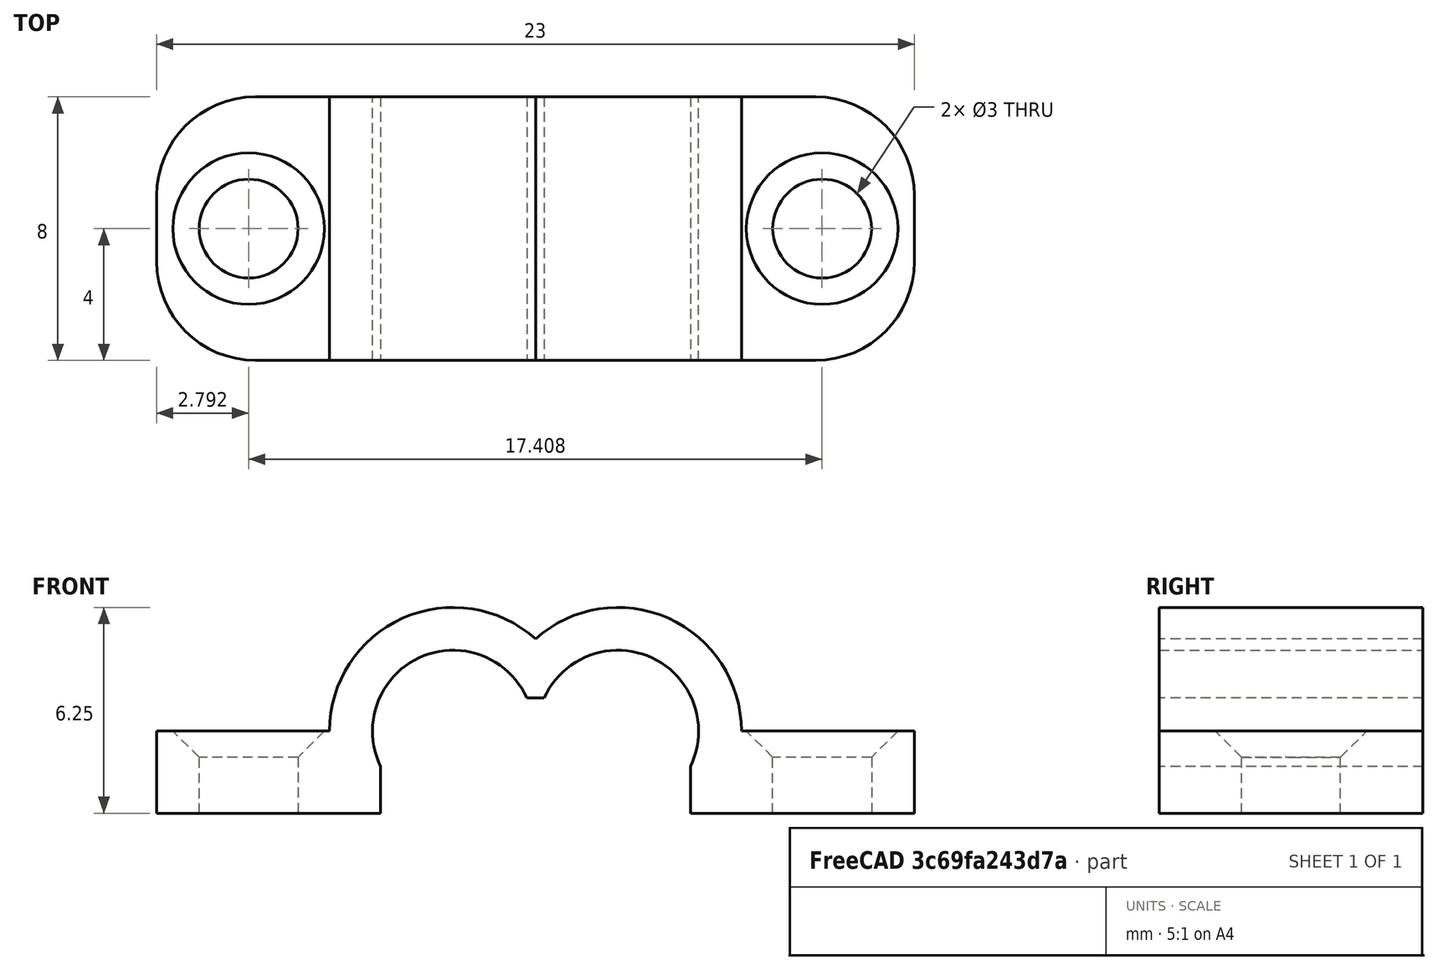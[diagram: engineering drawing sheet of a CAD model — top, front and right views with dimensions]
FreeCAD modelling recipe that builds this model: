
FCSTD DOCUMENT  (FreeCAD 0.21R32110 (Git))
Label: 2Cable_Clip_4_7mm
License: All rights reserved
LicenseURL: http://en.wikipedia.org/wiki/All_rights_reserved
objects: Sketcher::SketchObject×2, PartDesign::Pad×1, PartDesign::Pocket×1, PartDesign::Chamfer×1, PartDesign::Fillet×1, PartDesign::Body×1, App::Part×1
note: 11 computed .brp shape members not serialized (recipe doc carries the construction recipe); baked Part::Feature solids carry a one-line shape summary decoded from their .brp

FEATURE [Sketcher::SketchObject] Sketch
  FullyConstrained = false
  MapMode = 5
  Placement = pos=(0,0,0) rot=(1,0,0;1.5708rad)
  Support = -> [XZ_Plane001]
  sketch-geometry (14):
    g0: ArcOfCircle CenterX=9.25 CenterY=2.5 CenterZ=0 NormalX=0 NormalY=0 NormalZ=1 AngleXU=0 Radius=2.45 StartAngle=0.420441 EndAngle=3.14159
    g1: LineSegment StartX=0 StartY=0 StartZ=0 EndX=6.8 EndY=0 EndZ=0
    g2: LineSegment StartX=23.5 StartY=0 StartZ=0 EndX=23.5 EndY=2.5 EndZ=0
    g3: LineSegment StartX=0 StartY=2.5 StartZ=0 EndX=0 EndY=0 EndZ=0
    g4: LineSegment StartX=5.25 StartY=2.5 StartZ=0 EndX=0 EndY=2.5 EndZ=0
    g5: LineSegment StartX=6.8 StartY=2.5 StartZ=0 EndX=6.8 EndY=0 EndZ=0
    g6: LineSegment StartX=16.7 StartY=0 StartZ=0 EndX=23.5 EndY=0 EndZ=0
    g7: LineSegment StartX=10 StartY=3.5 StartZ=0 EndX=20 EndY=3.5 EndZ=0
    g8: ArcOfCircle CenterX=14.25 CenterY=2.5 CenterZ=0 NormalX=0 NormalY=0 NormalZ=1 AngleXU=0 Radius=2.45 StartAngle=4.07627e-08 EndAngle=2.72115
    g9: LineSegment StartX=23.5 StartY=2.5 StartZ=0 EndX=18.25 EndY=2.5 EndZ=0
    g10: ArcOfCircle CenterX=9.25 CenterY=2.5 CenterZ=0 NormalX=0 NormalY=0 NormalZ=1 AngleXU=0 Radius=4 StartAngle=0.895665 EndAngle=3.14159
    g11: LineSegment StartX=16.7 StartY=0 StartZ=0 EndX=16.7 EndY=2.5 EndZ=0
    g12: LineSegment StartX=11.4866 StartY=3.5 StartZ=0 EndX=11.7634 EndY=3.5 EndZ=0
    g13: ArcOfCircle CenterX=14.25 CenterY=2.5 CenterZ=0 NormalX=0 NormalY=0 NormalZ=1 AngleXU=0 Radius=4 StartAngle=0 EndAngle=2.24593
  constraints (42):
    c: Diameter(g0) = 4.9
    c: Coincident(g6,g2)
    c: Coincident(g4,g3)
    c: Coincident(g3,g1)
    c: Horizontal(g1)
    c: Vertical(g2)
    c: Vertical(g3)
    c: Coincident(g1,g-1)
    c: Coincident(g4,g10)
    c: Vertical(g5)
    c: Coincident(g5,g0)
    c: Coincident(g5,g1)
    c: Distance(g3) = 2.5
    c: Equal(g3,g2)
    c: DistanceY(g0) = 2.5
    c: Horizontal(g6)
    c: Horizontal(g4)
    c: Horizontal(g7)
    c: Coincident(g9,g2)
    c: Horizontal(g9)
    c: Distance(g1) = 6.8
    c: Equal(g1,g6)
    c: PointOnObject(g12,g7)
    c: PointOnObject(g0,g7)
    c: Equal(g4,g9)
    c: Distance(g4) = 5.25
    c: Horizontal(g1,g6)
    c: Coincident(g10,g0)
    c: Coincident(g11,g6)
    c: Vertical(g11)
    c: PointOnObject(g8,g7)
    c: Coincident(g8,g11)
    c: Coincident(g12,g0)
    c: DistanceY(g7) = 3.5
    c: Equal(g0,g8)
    c: Horizontal(g0,g8)
    c: Distance(g0,g8) = 5
    c: Coincident(g13,g8)
    c: Coincident(g13,g10)
    c: Coincident(g13,g9)
    c: Equal(g10,g13)
    c: DistanceX(g0) = 9.25
FEATURE [PartDesign::Pad] Pad
  Direction = (0,-1,-2e-16)
  Length = 8
  Length2 = 10
  Placement = pos=(0,0,0) rot=(1,0,0;1.5708rad)
  Profile = -> Sketch
  ReferenceAxis = -> Sketch [N_Axis]
  Type = 0
FEATURE [Sketcher::SketchObject] Sketch001
  AttachmentOffset = pos=(0,0,2.5) rot=(0,0,1;0rad)
  FullyConstrained = false
  MapMode = 5
  Placement = pos=(0,0,2.5) rot=(0,0,1;0rad)
  Support = -> [XY_Plane001]
  sketch-geometry (2):
    g0: Circle CenterX=2.79203 CenterY=-4 CenterZ=0 NormalX=0 NormalY=0 NormalZ=1 AngleXU=0 Radius=1.5
    g1: Circle CenterX=20.2 CenterY=-4 CenterZ=0 NormalX=0 NormalY=0 NormalZ=1 AngleXU=0 Radius=1.5
  constraints (3):
    c: Equal(g0,g1)
    c: Diameter(g0) = 3
    c: DistanceY(g0) = -4
FEATURE [PartDesign::Pocket] Pocket
  BaseFeature = -> Pad
  Direction = (0,0,-1)
  Length = 5
  Length2 = 5
  Placement = pos=(0,0,0) rot=(1,0,0;1.5708rad)
  Profile = -> Sketch001
  ReferenceAxis = -> Sketch001 [N_Axis]
  Type = 1
FEATURE [PartDesign::Chamfer] Chamfer
  Angle = 45
  Base = -> Pocket [Edge36,Edge40]
  BaseFeature = -> Pocket
  ChamferType = 0
  FlipDirection = false
  Placement = pos=(0,0,0) rot=(1,0,0;1.5708rad)
  Size = 0.8
  Size2 = 1
  SupportTransform = false
  UseAllEdges = false
FEATURE [PartDesign::Fillet] Fillet
  Base = -> Chamfer [Edge25,Edge28,Edge17,Edge14]
  BaseFeature = -> Chamfer
  Placement = pos=(0,0,0) rot=(1,0,0;1.5708rad)
  Radius = 3
  SupportTransform = false
  UseAllEdges = false
FEATURE [PartDesign::Body] Body
  Group = -> [Sketch,Pad,Sketch001,Pocket,Chamfer,Fillet]
  Origin = -> Origin001
  Tip = -> Fillet
FEATURE [App::Part] Part
  Group = -> [Body]
  Origin = -> Origin
